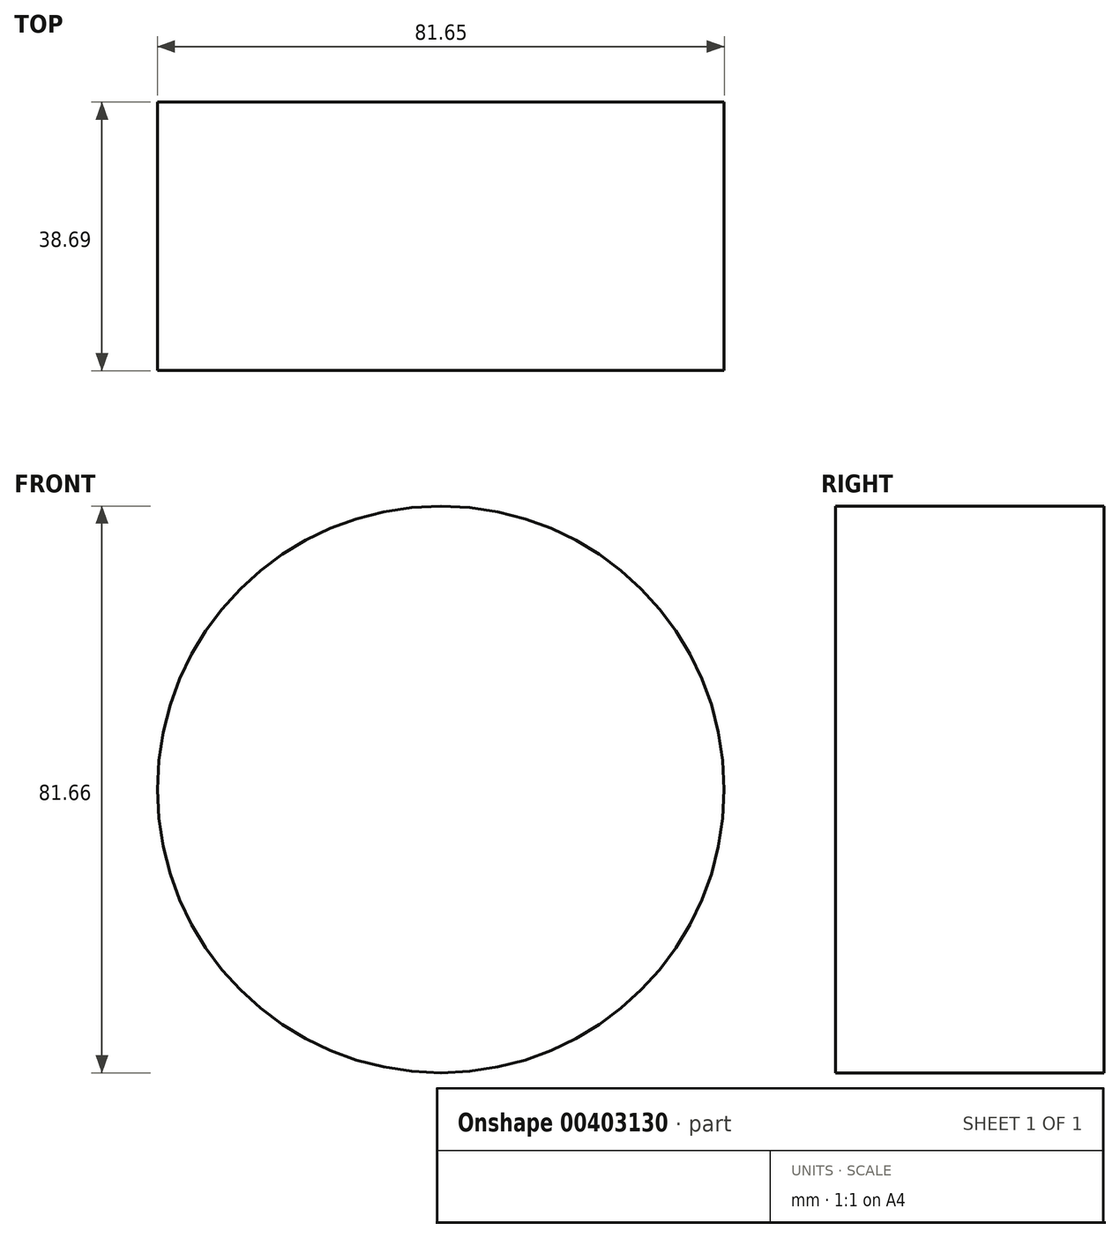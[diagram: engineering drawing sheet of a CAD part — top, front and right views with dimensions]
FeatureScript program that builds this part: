
annotation { "Feature Type Name" : "Feature", "Feature Type Description" : "" }
export const myFeature = defineFeature(function(context is Context, id is Id, definition is map)
    precondition{}
    {
        {
            var Q0;
            Q0=qCreatedBy(makeId("Front.planeOp"),FACE);
            var sketch = newSketch(context, id + "F0", { "sketchPlane" : qUnion([Q0])});
            skCircle(sketch, "E0", {"center": v(-0.02, -0.97) * mm, "radius": 40.83 * mm});
            skSolve(sketch);
        }
        {
            var Q0;
            Q0 = qSketchRegion(id + "F0", true);
            var Q1;
            Q1=sQuery(id+"F0.wireOp",EDGE,"E0");
            extrude(context, id + "F1", {"entities" : qUnion([Q0]), "bodyType" : ToolBodyType.SURFACE, "surfaceEntities" : qUnion([Q1]), "depth" : 38.69 * mm});
        }
    });
